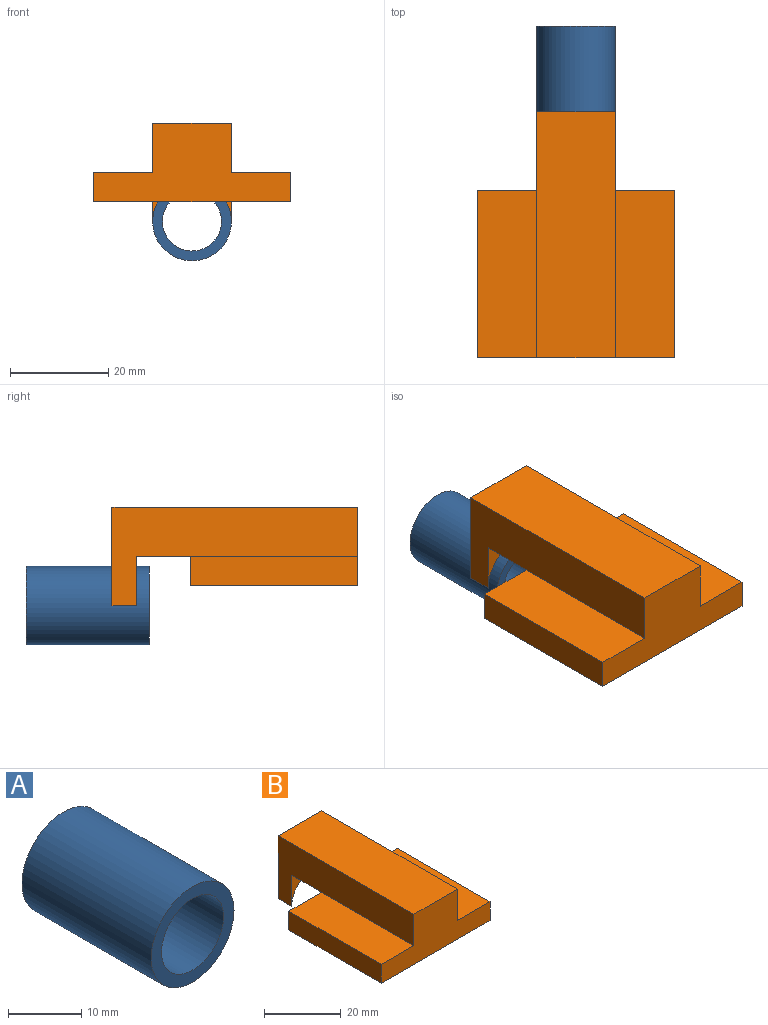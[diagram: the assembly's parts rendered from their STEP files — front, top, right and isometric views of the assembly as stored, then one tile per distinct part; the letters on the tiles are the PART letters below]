
ASSEMBLY  parts=2 mates=1
PART A: 4 faces, bbox 16x25x16 mm
  f0: cylinder r=6mm len=25mm, axis (0,1,0), area 942.5mm2, adj f2,f3
  f1: cylinder r=8mm len=25mm, axis (0,1,0), area 1256.6mm2, adj f2,f3
  f2: plane 16x16mm, normal (0,-1,0), area 88mm2, adj f0,f1
  f3: plane 16x16mm, normal (0,1,0), area 88mm2, adj f0,f1
PART B: 14 faces, bbox 40x50x20 mm
  f0: plane 50x20mm, normal (-1,0,0), area 550mm2, adj f1,f3,f4,f5,f6,f7,f13
  f1: plane 16x11mm, normal (0,0,-1), area 176mm2, adj f0,f2,f6,f9
  f2: plane 50x20mm, normal (1,0,0), area 550mm2, adj f1,f3,f4,f5,f6,f7,f8
  f3: plane 50x16mm, normal (0,0,1), area 800mm2, adj f0,f2,f4,f5
  f4: plane 40x16mm, normal (0,-1,0), area 400mm2, adj f0,f2,f3,f8,f10,f11,f12,f13
  f5: plane 20x16mm, normal (0,1,0), area 219.5mm2, adj f0,f2,f3,f7
  f6: plane 16x10mm, normal (0,-1,0), area 59.5mm2, adj f0,f1,f2,f7
  f7: cylinder r=8mm len=16mm, axis (0,1,0), area 125.7mm2, adj f0,f2,f5,f6
  f8: plane 34x12mm, normal (0,0,1), area 408mm2, adj f2,f4,f9,f10
  f9: plane 40x6mm, normal (0,1,0), area 240mm2, adj f1,f8,f10,f11,f12,f13
  f10: plane 34x6mm, normal (1,0,0), area 204mm2, adj f4,f8,f9,f12
  f11: plane 34x6mm, normal (-1,0,0), area 204mm2, adj f4,f9,f12,f13
  f12: plane 40x34mm, normal (0,0,-1), area 1360mm2, adj f4,f9,f10,f11
  f13: plane 34x12mm, normal (0,0,1), area 408mm2, adj f0,f4,f9,f11
PLACE A t=(-21.6,31.17,-6.46)mm
PLACE B t=(-21.6,13.7,-6.46)mm
MATE slider A.f0 <-> B.f7  axis (0,1,0) through (-21.6,18.67,-6.46)mm
